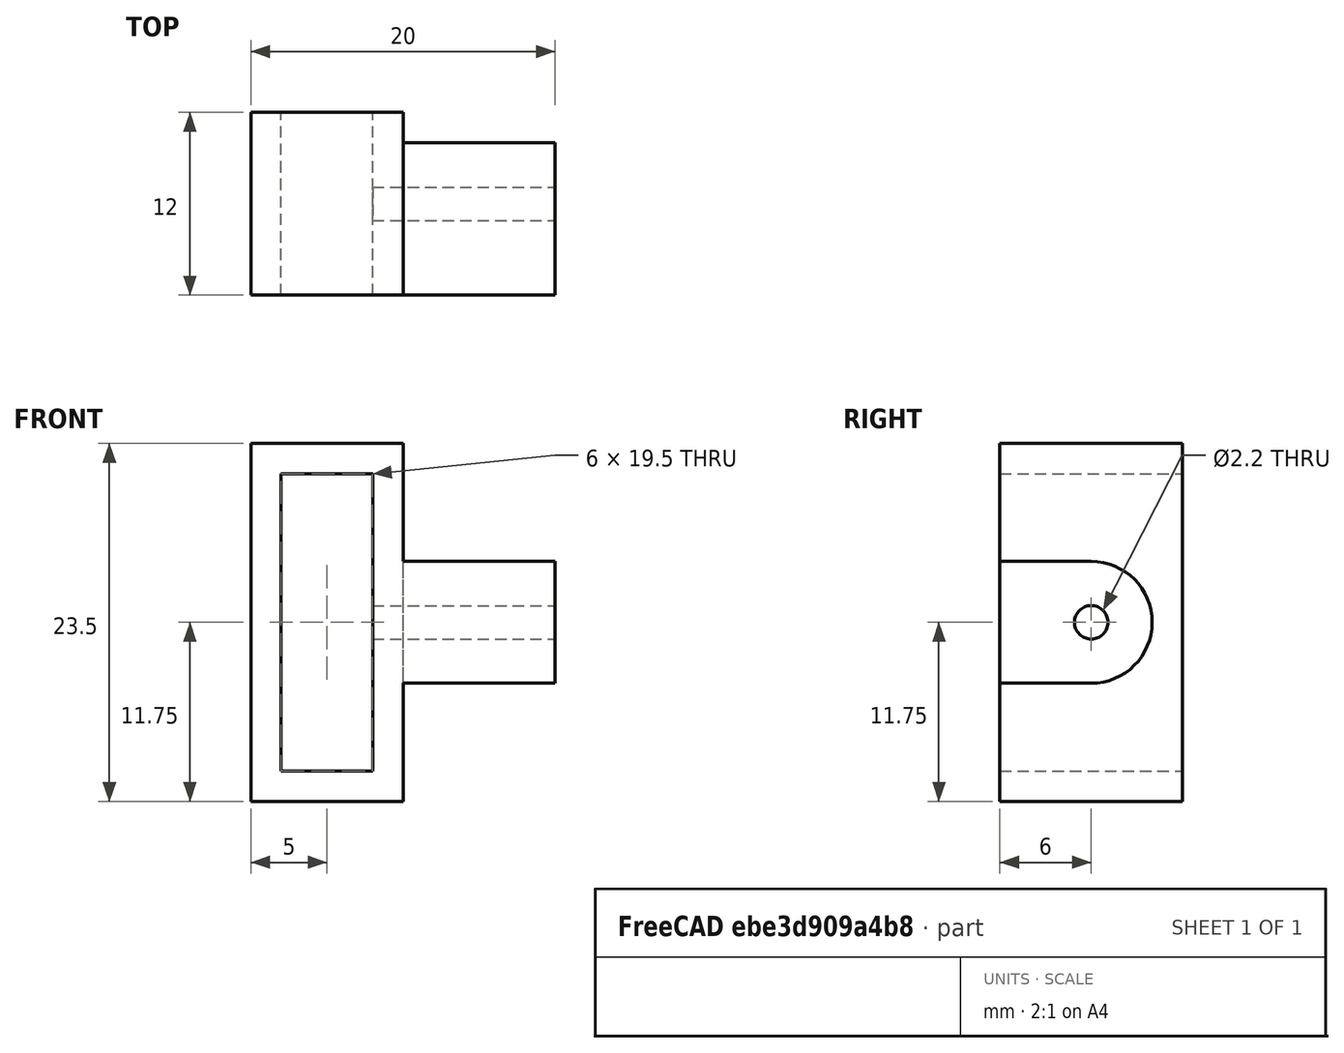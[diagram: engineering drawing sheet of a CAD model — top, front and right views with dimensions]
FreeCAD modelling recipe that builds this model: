
FCSTD DOCUMENT  (FreeCAD 0.16R6707 (Git))
Label: xmaxx-bumber-holder
License: All rights reserved
LicenseURL: http://en.wikipedia.org/wiki/All_rights_reserved
objects: Part::Box×3, Part::Cut×2, Part::Cylinder×2, Part::MultiFuse×2
note: 9 computed .brp shape members not serialized (recipe doc carries the construction recipe); baked Part::Feature solids carry a one-line shape summary decoded from their .brp

FEATURE [Part::Box] Box  label="Cube"
  Height = 23.5
  Length = 10
  Width = 12
FEATURE [Part::Box] Box001  label="Cube001"
  Height = 19.5
  Length = 6
  Placement = pos=(2,0,2) rot=(0,0,1;0rad)
  Width = 12
FEATURE [Part::Cut] Cut
  Base = -> Box
  Tool = -> Box001
FEATURE [Part::Cylinder] Cylinder
  Angle = 360
  Height = 10
  Placement = pos=(10,6,11.75) rot=(0,1,0;1.5708rad)
  Radius = 4
FEATURE [Part::Cylinder] Cylinder001
  Angle = 360
  Height = 15
  Placement = pos=(7,6,11.75) rot=(0,1,0;1.5708rad)
  Radius = 1.1
FEATURE [Part::MultiFuse] Fusion
  Shapes = -> [Cut,Cylinder]
FEATURE [Part::Box] Box002  label="Cube002"
  Height = 8
  Length = 10
  Placement = pos=(10,0,7.75) rot=(0,0,1;0rad)
  Width = 6
FEATURE [Part::MultiFuse] Fusion001
  Shapes = -> [Fusion,Box002]
FEATURE [Part::Cut] Cut001
  Base = -> Fusion001
  Tool = -> Cylinder001
